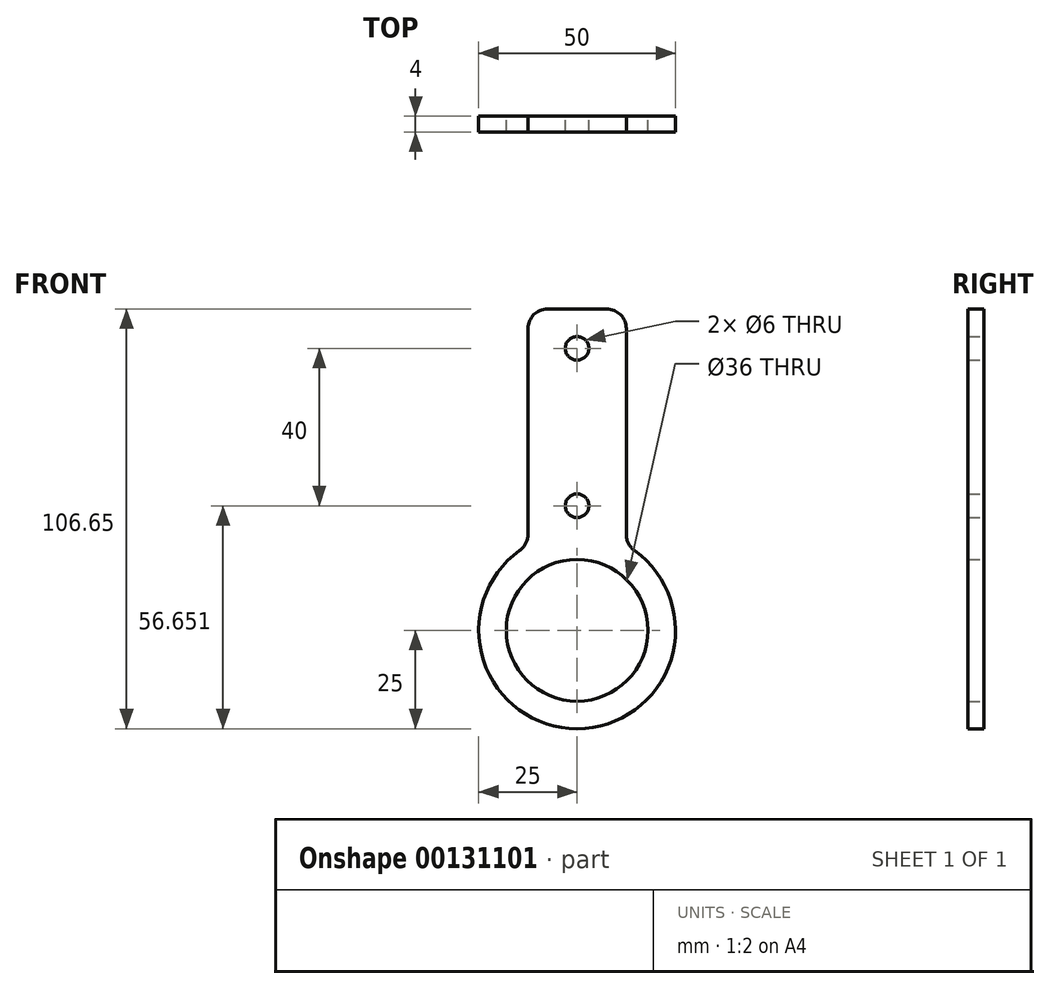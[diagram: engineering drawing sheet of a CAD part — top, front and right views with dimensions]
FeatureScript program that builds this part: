
annotation { "Feature Type Name" : "Feature", "Feature Type Description" : "" }
export const myFeature = defineFeature(function(context is Context, id is Id, definition is map)
    precondition{}
    {
        {
            var Q0;
            Q0=qCreatedBy(makeId("Front.planeOp"),FACE);
            var sketch = newSketch(context, id + "F0", { "sketchPlane" : qUnion([Q0])});
            skCircle(sketch, "E0", {"center": v(0, 0) * mm, "radius": 18 * mm});
            skArc(sketch, "E1", {"start": v(-12.5, 21.65) * mm, "mid": v(0, -25) * mm, "end": v(12.5, 21.65) * mm});
            skLineSegment(sketch, "E2.bottom", {"start": v(12.5, 21.65) * mm, "end": v(-12.5, 21.65) * mm, "construction": true});
            skLineSegment(sketch, "E2.top", {"start": v(12.5, 81.65) * mm, "end": v(-12.5, 81.65) * mm});
            skLineSegment(sketch, "E2.left", {"start": v(12.5, 21.65) * mm, "end": v(12.5, 81.65) * mm});
            skLineSegment(sketch, "E2.right", {"start": v(-12.5, 21.65) * mm, "end": v(-12.5, 81.65) * mm});
            skPoint(sketch, "E3", {"position": v(0, 31.65) * mm});
            skPoint(sketch, "E3.positionSnap0", {"position": v(0, 21.65) * mm});
            skPoint(sketch, "E4", {"position": v(0, 71.65) * mm});
            skSolve(sketch);
        }
        {
            var Q0;
            Q0=makeQuery(id+"F0.imprint","IMPRINT",FACE,{"disambiguationData":[TD([[makeQuery(id+"F0.imprint","IMPRINT",EDGE,{"derivedFrom":sQuery(id+"F0.wireOp",EDGE,"E0")}),-1.0]])]});
            extrude(context, id + "F1", {"entities" : qUnion([Q0]), "depth" : 4 * mm});
        }
        {
            var Q0;
            Q0=makeQuery(id+"F1.opExtrude","SWEPT_EDGE",EDGE,{"disambiguationData":[OSD([sQuery(id+"F0.wireOp",EDGE,"E2.top"),sQuery(id+"F0.wireOp",EDGE,"E2.left")])]});
            var Q1;
            Q1=makeQuery(id+"F1.opExtrude","SWEPT_EDGE",EDGE,{"disambiguationData":[OSD([sQuery(id+"F0.wireOp",EDGE,"E1"),sQuery(id+"F0.wireOp",EDGE,"E2.left")])]});
            var Q2;
            Q2=makeQuery(id+"F1.opExtrude","SWEPT_EDGE",EDGE,{"disambiguationData":[OSD([sQuery(id+"F0.wireOp",EDGE,"E1"),sQuery(id+"F0.wireOp",EDGE,"E2.right")])]});
            var Q3;
            Q3=makeQuery(id+"F1.opExtrude","SWEPT_EDGE",EDGE,{"disambiguationData":[OSD([sQuery(id+"F0.wireOp",EDGE,"E2.top"),sQuery(id+"F0.wireOp",EDGE,"E2.right")])]});
            fillet(context, id + "F2", {"entities" : qUnion([Q0, Q1, Q2, Q3]), "radius" : 5 * mm, "tangentPropagation" : true, "allowEdgeOverflow" : false});
        }
        {
            var Q0;
            Q0=sQuery(id+"F0.wireOp",VERTEX,"E3");
            var Q1;
            Q1=sQuery(id+"F0.wireOp",VERTEX,"E4");
            var Q2;
            Q2=makeQuery(id+"F1.opExtrude","SWEPT_BODY",BODY,{"disambiguationData":[OSD([sQuery(id+"F0.wireOp",EDGE,"E0"),sQuery(id+"F0.wireOp",EDGE,"E1"),sQuery(id+"F0.wireOp",EDGE,"E2.top"),sQuery(id+"F0.wireOp",EDGE,"E2.left"),sQuery(id+"F0.wireOp",EDGE,"E2.right")])]});
            hole(context, id + "F3", {"style" : HoleStyle.SIMPLE, "endStyle" : HoleEndStyle.THROUGH, "oppositeDirection" : true, "holeDiameter" : 6 * mm, "locations" : qUnion([Q0, Q1]), "scope" : qUnion([Q2]), "isTappedThrough" : true});
        }
    });
